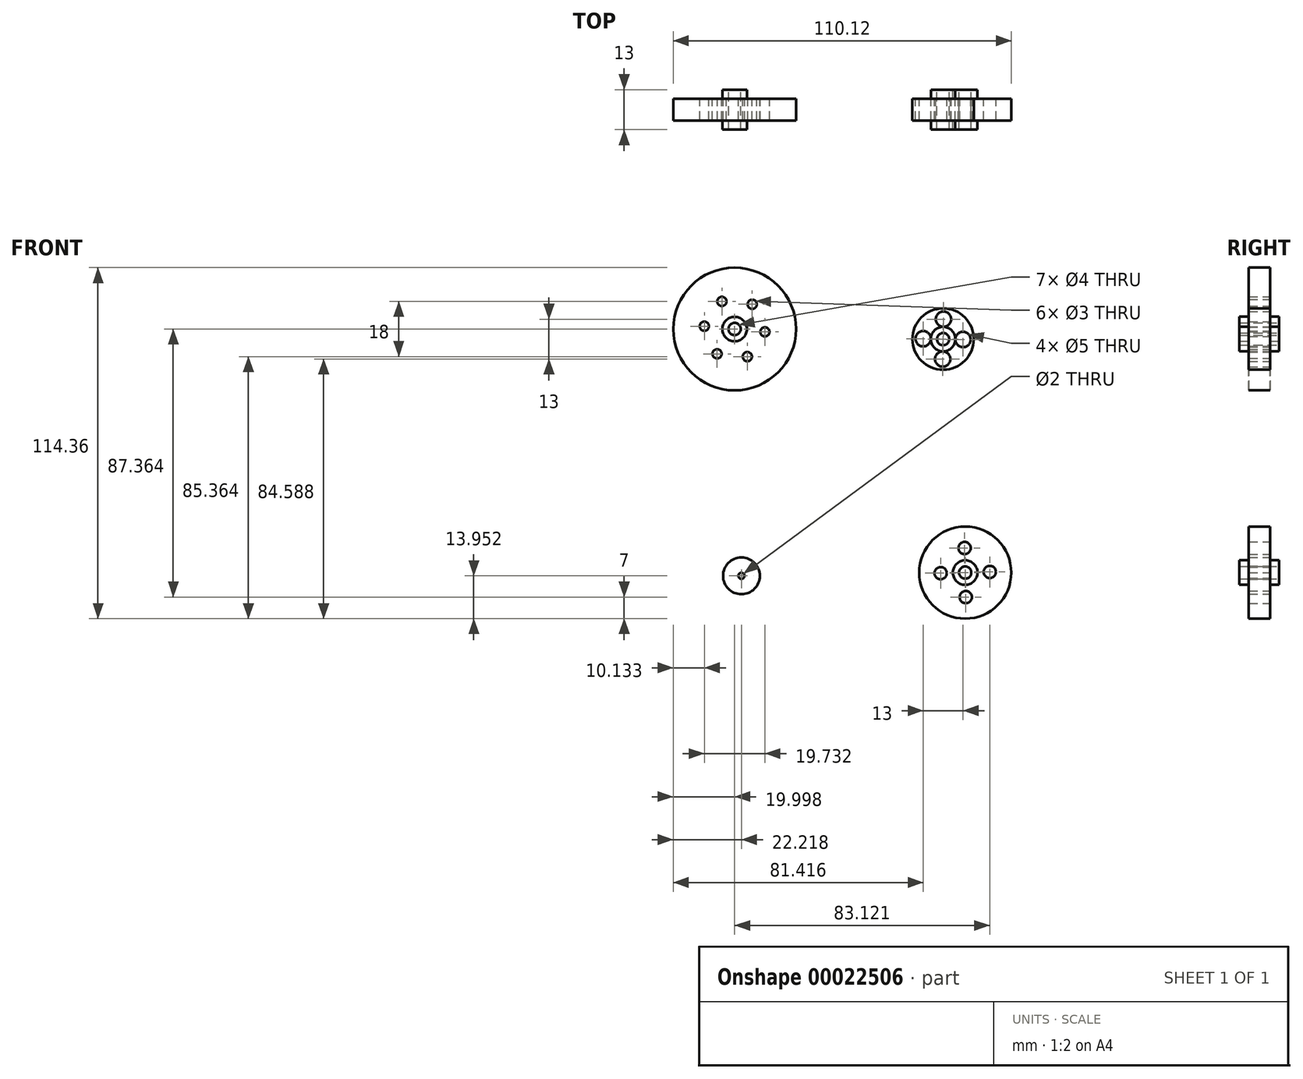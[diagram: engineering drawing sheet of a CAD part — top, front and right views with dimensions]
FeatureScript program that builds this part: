
annotation { "Feature Type Name" : "Feature", "Feature Type Description" : "" }
export const myFeature = defineFeature(function(context is Context, id is Id, definition is map)
    precondition{}
    {
        {
            var Q0;
            Q0=qCreatedBy(makeId("Front.planeOp"),FACE);
            var sketch = newSketch(context, id + "F0", { "sketchPlane" : qUnion([Q0])});
            skCircle(sketch, "E0", {"center": v(-38, 41.84) * mm, "radius": 20 * mm});
            skCircle(sketch, "E1", {"center": v(-42.14, 50.84) * mm, "radius": 1.5 * mm});
            skCircle(sketch, "E2.1.0", {"center": v(-47.87, 42.76) * mm, "radius": 1.5 * mm});
            skCircle(sketch, "E2.2.0", {"center": v(-43.72, 33.76) * mm, "radius": 1.5 * mm});
            skCircle(sketch, "E2.3.0", {"center": v(-33.86, 32.84) * mm, "radius": 1.5 * mm});
            skCircle(sketch, "E2.4.0", {"center": v(-28.14, 40.93) * mm, "radius": 1.5 * mm});
            skCircle(sketch, "E2.5.0", {"center": v(-32.28, 49.93) * mm, "radius": 1.5 * mm});
            skCircle(sketch, "E3", {"center": v(-38, 41.84) * mm, "radius": 4 * mm});
            skCircle(sketch, "E4", {"center": v(-38, 41.84) * mm, "radius": 2 * mm});
            skSolve(sketch);
        }
        {
            var Q0;
            Q0=makeQuery(id+"F0.imprint","IMPRINT",FACE,{"disambiguationData":[TD([[makeQuery(id+"F0.imprint","IMPRINT",EDGE,{"derivedFrom":sQuery(id+"F0.wireOp",EDGE,"E0")}),1.0]])]});
            extrude(context, id + "F1", {"entities" : qUnion([Q0]), "depth" : 7 * mm});
        }
        {
            var Q0;
            Q0=makeQuery(id+"F0.imprint","IMPRINT",FACE,{"disambiguationData":[TD([[makeQuery(id+"F0.imprint","IMPRINT",EDGE,{"derivedFrom":sQuery(id+"F0.wireOp",EDGE,"E3")}),1.0]])]});
            extrude(context, id + "F2", {"entities" : qUnion([Q0]), "operationType" : NewBodyOperationType.ADD, "depth" : 10 * mm, "hasSecondDirection" : true, "secondDirectionOppositeDirection" : true, "secondDirectionDepth" : 3 * mm});
        }
        {
            var Q0;
            Q0=qCreatedBy(makeId("Front.planeOp"),FACE);
            var sketch = newSketch(context, id + "F3", { "sketchPlane" : qUnion([Q0])});
            skCircle(sketch, "E5", {"center": v(29.92, 38.57) * mm, "radius": 10 * mm});
            skCircle(sketch, "E6", {"center": v(29.92, 38.57) * mm, "radius": 4 * mm});
            skCircle(sketch, "E7", {"center": v(30.04, 45.07) * mm, "radius": 2.5 * mm});
            skCircle(sketch, "E8.1.0", {"center": v(23.42, 38.7) * mm, "radius": 2.5 * mm});
            skCircle(sketch, "E8.2.0", {"center": v(29.79, 32.07) * mm, "radius": 2.5 * mm});
            skCircle(sketch, "E8.3.0", {"center": v(36.42, 38.44) * mm, "radius": 2.5 * mm});
            skCircle(sketch, "E9", {"center": v(29.92, 38.57) * mm, "radius": 2 * mm});
            skSolve(sketch);
        }
        {
            var Q0;
            Q0=makeQuery(id+"F3.imprint","IMPRINT",FACE,{"disambiguationData":[TD([[makeQuery(id+"F3.imprint","IMPRINT",EDGE,{"derivedFrom":sQuery(id+"F3.wireOp",EDGE,"E5")}),1.0]])]});
            extrude(context, id + "F4", {"entities" : qUnion([Q0]), "depth" : 7 * mm});
        }
        {
            var Q0;
            Q0=makeQuery(id+"F3.imprint","IMPRINT",FACE,{"disambiguationData":[TD([[makeQuery(id+"F3.imprint","IMPRINT",EDGE,{"derivedFrom":sQuery(id+"F3.wireOp",EDGE,"E6")}),1.0]])]});
            extrude(context, id + "F5", {"entities" : qUnion([Q0]), "operationType" : NewBodyOperationType.ADD, "depth" : 10 * mm});
        }
        {
            var Q0;
            Q0=makeQuery(id+"F3.imprint","IMPRINT",FACE,{"disambiguationData":[TD([[makeQuery(id+"F3.imprint","IMPRINT",EDGE,{"derivedFrom":sQuery(id+"F3.wireOp",EDGE,"E6")}),1.0]])]});
            extrude(context, id + "F6", {"entities" : qUnion([Q0]), "operationType" : NewBodyOperationType.ADD, "oppositeDirection" : true, "depth" : 3 * mm});
        }
        {
            var Q0;
            Q0=qCreatedBy(makeId("Front.planeOp"),FACE);
            var sketch = newSketch(context, id + "F7", { "sketchPlane" : qUnion([Q0])});
            skCircle(sketch, "E10", {"center": v(-35.78, -38.57) * mm, "radius": 6 * mm});
            skCircle(sketch, "E11", {"center": v(-35.78, -38.57) * mm, "radius": 1 * mm});
            skSolve(sketch);
        }
        {
            var Q0;
            Q0=makeQuery(id+"F7.imprint","IMPRINT",FACE,{"disambiguationData":[TD([[makeQuery(id+"F7.imprint","IMPRINT",EDGE,{"derivedFrom":sQuery(id+"F7.wireOp",EDGE,"E10")}),1.0]])]});
            extrude(context, id + "F8", {"entities" : qUnion([Q0]), "depth" : 7 * mm});
        }
        {
            var Q0;
            Q0=qCreatedBy(makeId("Front.planeOp"),FACE);
            var sketch = newSketch(context, id + "F9", { "sketchPlane" : qUnion([Q0])});
            skCircle(sketch, "E12", {"center": v(37.12, -37.52) * mm, "radius": 15 * mm});
            skCircle(sketch, "E13", {"center": v(36.92, -29.52) * mm, "radius": 2 * mm});
            skCircle(sketch, "E14", {"center": v(37.12, -37.52) * mm, "radius": 2 * mm});
            skCircle(sketch, "E15", {"center": v(37.12, -37.52) * mm, "radius": 4 * mm});
            skCircle(sketch, "E16.1.0", {"center": v(29.12, -37.72) * mm, "radius": 2 * mm});
            skCircle(sketch, "E16.2.0", {"center": v(37.32, -45.52) * mm, "radius": 2 * mm});
            skCircle(sketch, "E16.3.0", {"center": v(45.12, -37.32) * mm, "radius": 2 * mm});
            skSolve(sketch);
        }
        {
            var Q0;
            Q0=makeQuery(id+"F9.imprint","IMPRINT",FACE,{"disambiguationData":[TD([[makeQuery(id+"F9.imprint","IMPRINT",EDGE,{"derivedFrom":sQuery(id+"F9.wireOp",EDGE,"E12")}),1.0]])]});
            extrude(context, id + "F10", {"entities" : qUnion([Q0]), "depth" : 7 * mm});
        }
        {
            var Q0;
            Q0=makeQuery(id+"F9.imprint","IMPRINT",FACE,{"disambiguationData":[TD([[makeQuery(id+"F9.imprint","IMPRINT",EDGE,{"derivedFrom":sQuery(id+"F9.wireOp",EDGE,"E14")}),-1.0]])]});
            extrude(context, id + "F11", {"entities" : qUnion([Q0]), "operationType" : NewBodyOperationType.ADD, "depth" : 10 * mm, "hasSecondDirection" : true, "secondDirectionOppositeDirection" : true, "secondDirectionDepth" : 3 * mm});
        }
    });
